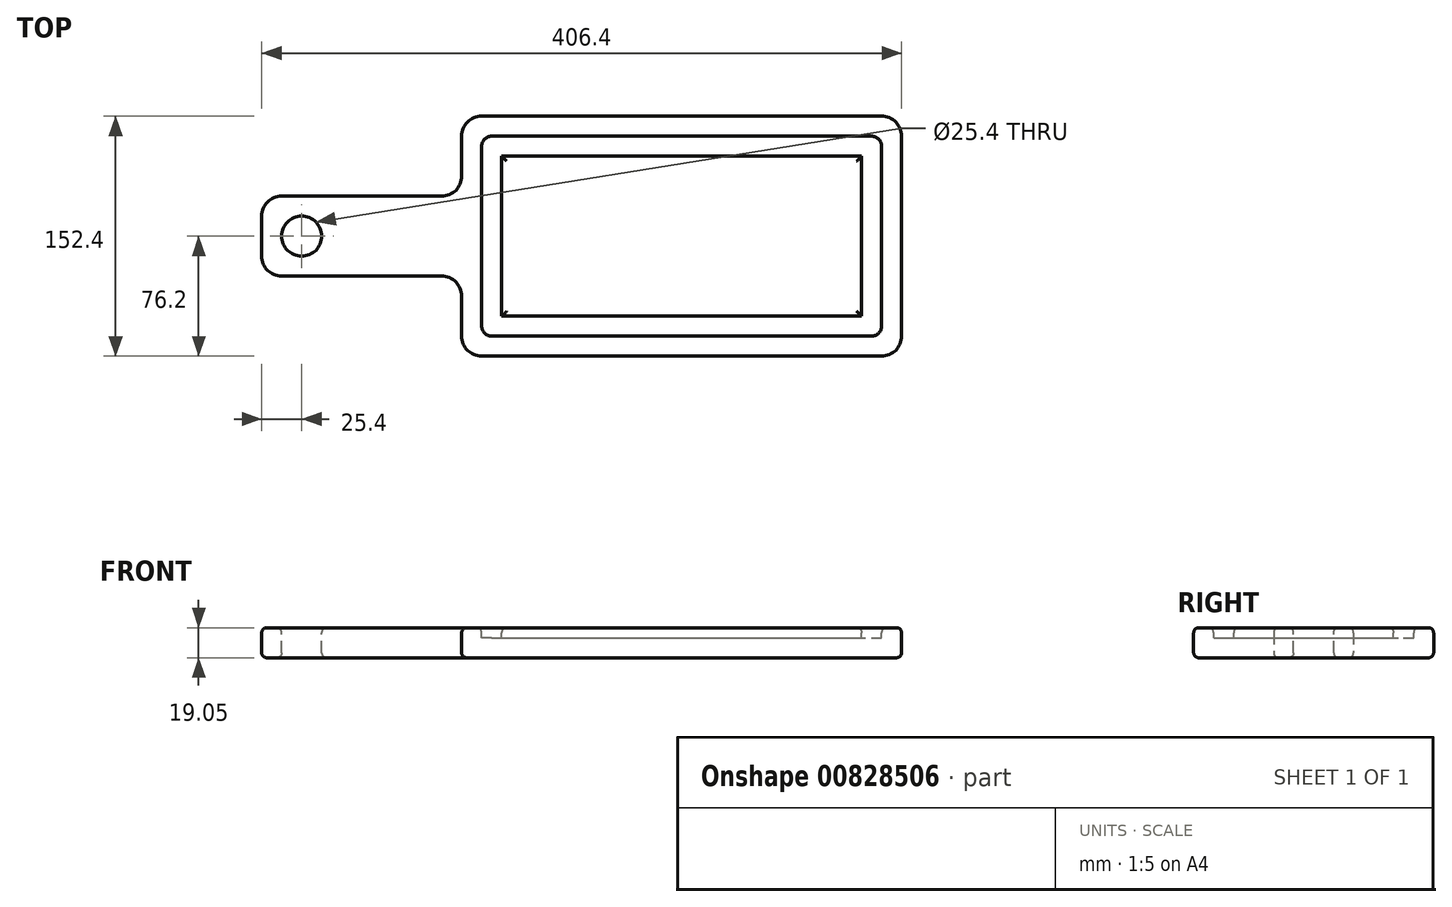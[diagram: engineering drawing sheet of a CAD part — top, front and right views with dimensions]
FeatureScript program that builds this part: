
annotation { "Feature Type Name" : "Feature", "Feature Type Description" : "" }
export const myFeature = defineFeature(function(context is Context, id is Id, definition is map)
    precondition{}
    {
        {
            var Q0;
            Q0=qCreatedBy(makeId("Top.planeOp"),FACE);
            var sketch = newSketch(context, id + "F0", { "sketchPlane" : qUnion([Q0])});
            skLineSegment(sketch, "E0.bottom", {"start": v(0, 0) * mm, "end": v(279.4, 0) * mm});
            skLineSegment(sketch, "E0.top", {"start": v(0, 152.4) * mm, "end": v(279.4, 152.4) * mm});
            skLineSegment(sketch, "E0.left", {"start": v(0, 0) * mm, "end": v(0, 152.4) * mm});
            skLineSegment(sketch, "E0.right", {"start": v(279.4, 0) * mm, "end": v(279.4, 152.4) * mm});
            skLineSegment(sketch, "E1.bottom", {"start": v(0, 101.6) * mm, "end": v(-127, 101.6) * mm});
            skLineSegment(sketch, "E1.top", {"start": v(0, 50.8) * mm, "end": v(-127, 50.8) * mm});
            skLineSegment(sketch, "E1.left", {"start": v(0, 101.6) * mm, "end": v(0, 50.8) * mm});
            skLineSegment(sketch, "E1.right", {"start": v(-127, 101.6) * mm, "end": v(-127, 50.8) * mm});
            skSolve(sketch);
        }
        {
            var Q0;
            {var subQ3=sQuery(id+"F0.wireOp",EDGE,"E0.bottom");Q0=makeQuery(id+"F0.imprint","IMPRINT",FACE,{"disambiguationData":[TD([[makeQuery(id+"F0.imprint","IMPRINT",EDGE,{"derivedFrom":subQ3}),1.0]])]});}
            var Q1;
            Q1=makeQuery(id+"F0.imprint","IMPRINT",FACE,{"disambiguationData":[TD([[makeQuery(id+"F0.imprint","IMPRINT",EDGE,{"derivedFrom":sQuery(id+"F0.wireOp",EDGE,"E1.bottom")}),1.0]])]});
            extrude(context, id + "F1", {"entities" : qUnion([Q0, Q1]), "depth" : 19.05 * mm, "offsetDistance" : 25.4 * mm});
        }
        {
            var Q0;
            Q0=makeQuery(id+"F1.opExtrude","CAP_FACE",FACE,{"disambiguationData":[OSD([sQuery(id+"F0.wireOp",EDGE,"E0.bottom"),sQuery(id+"F0.wireOp",EDGE,"E0.top"),sQuery(id+"F0.wireOp",EDGE,"E0.left"),sQuery(id+"F0.wireOp",EDGE,"E0.right"),sQuery(id+"F0.wireOp",EDGE,"E1.bottom"),sQuery(id+"F0.wireOp",EDGE,"E1.top"),sQuery(id+"F0.wireOp",EDGE,"E1.right")])],"isStart":false});
            var sketch = newSketch(context, id + "F2", { "sketchPlane" : qUnion([Q0])});
            skCircle(sketch, "E2", {"center": v(-101.6, 76.2) * mm, "radius": 12.7 * mm});
            skSolve(sketch);
        }
        {
            var Q0;
            Q0 = qSketchRegion(id + "F2", true);
            extrude(context, id + "F3", {"entities" : qUnion([Q0]), "operationType" : NewBodyOperationType.REMOVE, "oppositeDirection" : true, "depth" : 25.4 * mm, "offsetDistance" : 25.4 * mm});
        }
        {
            var Q0;
            Q0=makeQuery(id+"F1.opExtrude","CAP_FACE",FACE,{"disambiguationData":[OSD([sQuery(id+"F0.wireOp",EDGE,"E0.bottom"),sQuery(id+"F0.wireOp",EDGE,"E0.top"),sQuery(id+"F0.wireOp",EDGE,"E0.left"),sQuery(id+"F0.wireOp",EDGE,"E0.right"),sQuery(id+"F0.wireOp",EDGE,"E1.bottom"),sQuery(id+"F0.wireOp",EDGE,"E1.top"),sQuery(id+"F0.wireOp",EDGE,"E1.right")])],"isStart":false});
            var sketch = newSketch(context, id + "F4", { "sketchPlane" : qUnion([Q0])});
            skLineSegment(sketch, "E3.0", {"start": v(12.7, 12.7) * mm, "end": v(12.7, 50.8) * mm});
            skLineSegment(sketch, "E3.1", {"start": v(12.7, 101.6) * mm, "end": v(12.7, 139.7) * mm});
            skLineSegment(sketch, "E3.2", {"start": v(12.7, 139.7) * mm, "end": v(266.7, 139.7) * mm});
            skLineSegment(sketch, "E3.3", {"start": v(266.7, 12.7) * mm, "end": v(266.7, 139.7) * mm});
            skLineSegment(sketch, "E3.4", {"start": v(12.7, 12.7) * mm, "end": v(266.7, 12.7) * mm});
            skLineSegment(sketch, "E4", {"start": v(12.7, 101.6) * mm, "end": v(12.7, 50.8) * mm});
            skLineSegment(sketch, "E5.0", {"start": v(25.4, 101.6) * mm, "end": v(25.4, 127) * mm});
            skLineSegment(sketch, "E5.1", {"start": v(254, 25.4) * mm, "end": v(254, 127) * mm});
            skLineSegment(sketch, "E5.2", {"start": v(25.4, 25.4) * mm, "end": v(254, 25.4) * mm});
            skLineSegment(sketch, "E5.3", {"start": v(25.4, 127) * mm, "end": v(254, 127) * mm});
            skLineSegment(sketch, "E5.4", {"start": v(25.4, 25.4) * mm, "end": v(25.4, 50.8) * mm});
            skLineSegment(sketch, "E5.5", {"start": v(25.4, 101.6) * mm, "end": v(25.4, 50.8) * mm});
            skSolve(sketch);
        }
        {
            var Q0;
            Q0=makeQuery(id+"F4.imprint","IMPRINT",FACE,{"disambiguationData":[TD([[makeQuery(id+"F4.imprint","IMPRINT",EDGE,{"derivedFrom":sQuery(id+"F4.wireOp",EDGE,"E3.0")}),-1.0]])]});
            extrude(context, id + "F5", {"entities" : qUnion([Q0]), "operationType" : NewBodyOperationType.REMOVE, "oppositeDirection" : true, "depth" : 6.35 * mm, "offsetDistance" : 25.4 * mm});
        }
        {
            var Q0;
            Q0=makeQuery(id+"F5.boolean.opBoolean","COPY",EDGE,{"derivedFrom":makeQuery(id+"F5.opExtrude","SWEPT_EDGE",EDGE,{"disambiguationData":[OSD([sQuery(id+"F4.wireOp",EDGE,"E3.1"),sQuery(id+"F4.wireOp",EDGE,"E3.2")])]})});
            var Q1;
            Q1=makeQuery(id+"F5.boolean.opBoolean","COPY",EDGE,{"derivedFrom":makeQuery(id+"F5.opExtrude","SWEPT_EDGE",EDGE,{"disambiguationData":[OSD([sQuery(id+"F4.wireOp",EDGE,"E3.0"),sQuery(id+"F4.wireOp",EDGE,"E3.4")])]})});
            var Q2;
            Q2=makeQuery(id+"F5.boolean.opBoolean","COPY",EDGE,{"derivedFrom":makeQuery(id+"F5.opExtrude","SWEPT_EDGE",EDGE,{"disambiguationData":[OSD([sQuery(id+"F4.wireOp",EDGE,"E3.2"),sQuery(id+"F4.wireOp",EDGE,"E3.3")])]})});
            var Q3;
            Q3=makeQuery(id+"F5.boolean.opBoolean","COPY",EDGE,{"derivedFrom":makeQuery(id+"F5.opExtrude","SWEPT_EDGE",EDGE,{"disambiguationData":[OSD([sQuery(id+"F4.wireOp",EDGE,"E3.3"),sQuery(id+"F4.wireOp",EDGE,"E3.4")])]})});
            fillet(context, id + "F6", {"entities" : qUnion([Q0, Q1, Q2, Q3]), "radius" : 6.35 * mm, "tangentPropagation" : true, "allowEdgeOverflow" : false});
        }
        {
            var Q0;
            Q0=makeQuery(id+"F1.opExtrude","SWEPT_EDGE",EDGE,{"disambiguationData":[OSD([sQuery(id+"F0.wireOp",EDGE,"E1.top"),sQuery(id+"F0.wireOp",EDGE,"E1.right")])]});
            var Q1;
            Q1=makeQuery(id+"F1.opExtrude","SWEPT_EDGE",EDGE,{"disambiguationData":[OSD([sQuery(id+"F0.wireOp",EDGE,"E0.bottom"),sQuery(id+"F0.wireOp",EDGE,"E0.left")])]});
            var Q2;
            Q2=makeQuery(id+"F1.opExtrude","SWEPT_EDGE",EDGE,{"disambiguationData":[OSD([sQuery(id+"F0.wireOp",EDGE,"E1.bottom"),sQuery(id+"F0.wireOp",EDGE,"E1.right")])]});
            var Q3;
            Q3=makeQuery(id+"F1.opExtrude","SWEPT_EDGE",EDGE,{"disambiguationData":[OSD([sQuery(id+"F0.wireOp",EDGE,"E0.top"),sQuery(id+"F0.wireOp",EDGE,"E0.left")])]});
            var Q4;
            Q4=makeQuery(id+"F1.opExtrude","SWEPT_EDGE",EDGE,{"disambiguationData":[OSD([sQuery(id+"F0.wireOp",EDGE,"E0.left"),sQuery(id+"F0.wireOp",EDGE,"E1.bottom"),sQuery(id+"F0.wireOp",EDGE,"E1.left")])]});
            var Q5;
            Q5=makeQuery(id+"F1.opExtrude","SWEPT_EDGE",EDGE,{"disambiguationData":[OSD([sQuery(id+"F0.wireOp",EDGE,"E0.left"),sQuery(id+"F0.wireOp",EDGE,"E1.top"),sQuery(id+"F0.wireOp",EDGE,"E1.left")])]});
            var Q6;
            Q6=makeQuery(id+"F1.opExtrude","SWEPT_EDGE",EDGE,{"disambiguationData":[OSD([sQuery(id+"F0.wireOp",EDGE,"E0.bottom"),sQuery(id+"F0.wireOp",EDGE,"E0.right")])]});
            var Q7;
            Q7=makeQuery(id+"F1.opExtrude","SWEPT_EDGE",EDGE,{"disambiguationData":[OSD([sQuery(id+"F0.wireOp",EDGE,"E0.top"),sQuery(id+"F0.wireOp",EDGE,"E0.right")])]});
            fillet(context, id + "F7", {"entities" : qUnion([Q0, Q1, Q2, Q3, Q4, Q5, Q6, Q7]), "radius" : 12.7 * mm, "tangentPropagation" : true, "allowEdgeOverflow" : false});
        }
        {
            var Q0;
            Q0=makeQuery(id+"F5.boolean.opBoolean","SPLIT",FACE,{"disambiguationData":[TD([makeQuery(id+"F5.opExtrude","SWEPT_FACE",FACE,{"disambiguationData":[OSD([sQuery(id+"F4.wireOp",EDGE,"E5.1")])]})])],"derivedFrom":makeQuery(id+"F1.opExtrude","CAP_FACE",FACE,{"disambiguationData":[OSD([sQuery(id+"F0.wireOp",EDGE,"E0.bottom"),sQuery(id+"F0.wireOp",EDGE,"E0.top"),sQuery(id+"F0.wireOp",EDGE,"E0.left"),sQuery(id+"F0.wireOp",EDGE,"E0.right"),sQuery(id+"F0.wireOp",EDGE,"E1.bottom"),sQuery(id+"F0.wireOp",EDGE,"E1.top"),sQuery(id+"F0.wireOp",EDGE,"E1.right")])],"isStart":false})});
            var Q1;
            {var subQ0=sQuery(id+"F0.wireOp",EDGE,"E1.right");var subQ1=sQuery(id+"F0.wireOp",EDGE,"E1.top");var subQ2=sQuery(id+"F0.wireOp",EDGE,"E1.bottom");var subQ3=sQuery(id+"F0.wireOp",EDGE,"E0.right");var subQ4=sQuery(id+"F0.wireOp",EDGE,"E0.bottom");var subQ5=sQuery(id+"F0.wireOp",EDGE,"E0.left");var subQ6=sQuery(id+"F0.wireOp",EDGE,"E0.top");Q1=makeQuery(id+"F5.boolean.opBoolean","SPLIT",FACE,{"disambiguationData":[TD([makeQuery(id+"F1.opExtrude","SWEPT_FACE",FACE,{"disambiguationData":[OSD([subQ4])]})])],"derivedFrom":makeQuery(id+"F1.opExtrude","CAP_FACE",FACE,{"disambiguationData":[OSD([subQ4,subQ6,subQ5,subQ3,subQ2,subQ1,subQ0])],"isStart":false})});}
            var Q2;
            Q2=makeQuery(id+"F1.opExtrude","CAP_FACE",FACE,{"disambiguationData":[OSD([sQuery(id+"F0.wireOp",EDGE,"E0.bottom"),sQuery(id+"F0.wireOp",EDGE,"E0.top"),sQuery(id+"F0.wireOp",EDGE,"E0.left"),sQuery(id+"F0.wireOp",EDGE,"E0.right"),sQuery(id+"F0.wireOp",EDGE,"E1.bottom"),sQuery(id+"F0.wireOp",EDGE,"E1.top"),sQuery(id+"F0.wireOp",EDGE,"E1.right")])],"isStart":true});
            fillet(context, id + "F8", {"entities" : qUnion([Q0, Q1, Q2]), "radius" : 3.17 * mm, "tangentPropagation" : true, "allowEdgeOverflow" : false});
        }
    });
